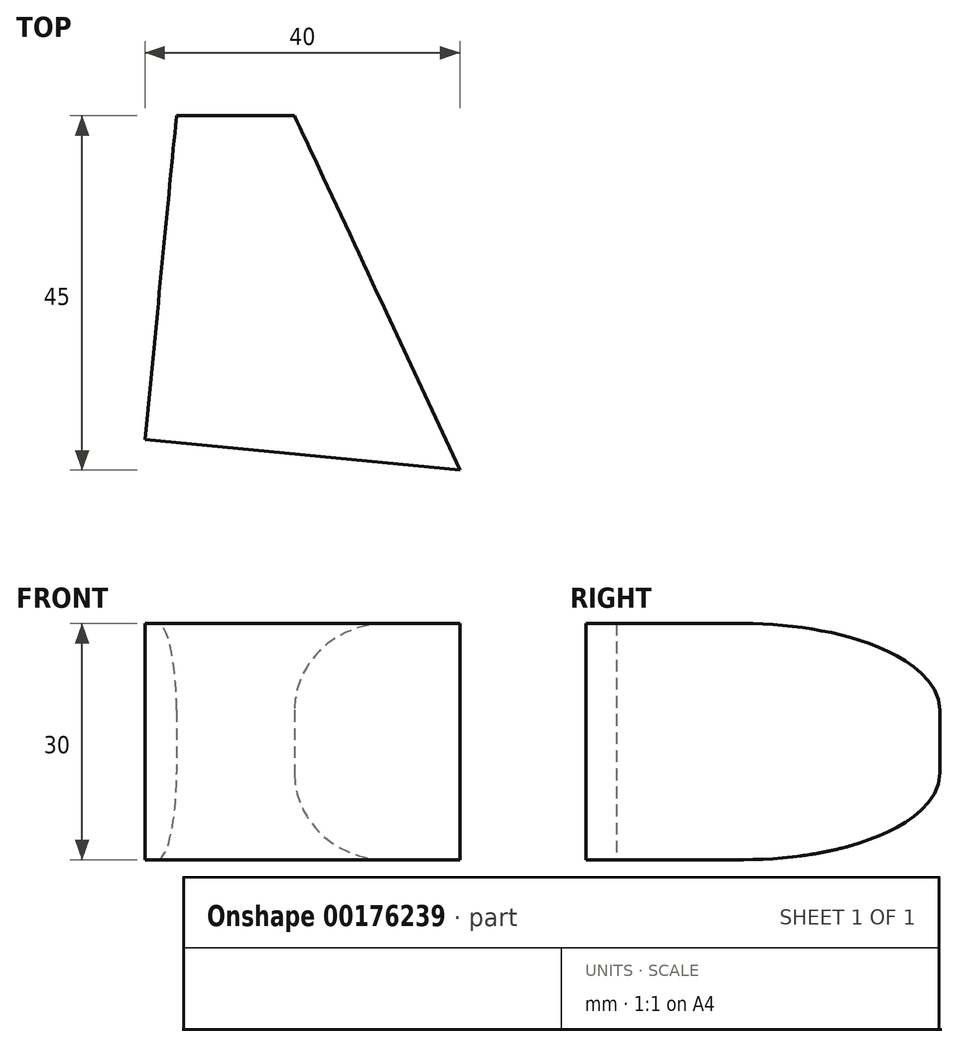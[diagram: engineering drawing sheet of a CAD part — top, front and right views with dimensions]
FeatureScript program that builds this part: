
annotation { "Feature Type Name" : "Feature", "Feature Type Description" : "" }
export const myFeature = defineFeature(function(context is Context, id is Id, definition is map)
    precondition{}
    {
        {
            var Q0;
            Q0=qCreatedBy(makeId("Top.planeOp"),FACE);
            var sketch = newSketch(context, id + "F0", { "sketchPlane" : qUnion([Q0])});
            skLineSegment(sketch, "E0", {"start": v(0, 20) * mm, "end": v(-15, 20) * mm});
            skLineSegment(sketch, "E1", {"start": v(-15, 20) * mm, "end": v(-19, -21.1) * mm});
            skLineSegment(sketch, "E2", {"start": v(-19, -21.1) * mm, "end": v(21, -25) * mm});
            skLineSegment(sketch, "E3", {"start": v(21, -25) * mm, "end": v(0, 20) * mm});
            skSolve(sketch);
        }
        {
            var Q0;
            Q0=qSketchRegion(id+"F0",true);
            extrude(context, id + "F1", {"entities" : qUnion([Q0]), "depth" : 15 * mm, "hasSecondDirection" : true, "secondDirectionOppositeDirection" : true, "secondDirectionDepth" : 15 * mm});
        }
        {
            var Q0;
            Q0=qCreatedBy(makeId("Right.planeOp"),FACE);
            var sketch = newSketch(context, id + "F2", { "sketchPlane" : qUnion([Q0])});
            skEllipticalArc(sketch, "E4", {});
            skLineSegment(sketch, "E5.0", {"start": v(20, 15) * mm, "end": v(20, -15) * mm, "construction": true});
            skPoint(sketch, "E6", {"position": v(20, -4) * mm});
            skPoint(sketch, "E7", {"position": v(-5, -15) * mm});
            skLineSegment(sketch, "E8", {"start": v(20, -4) * mm, "end": v(-5, -4) * mm, "construction": true});
            skLineSegment(sketch, "E9", {"start": v(-5, -15) * mm, "end": v(-5, -4) * mm, "construction": true});
            skEllipticalArc(sketch, "E10.MirrorCS", {});
            skLineSegment(sketch, "E11", {"start": v(-5, -15) * mm, "end": v(20, -15) * mm});
            skLineSegment(sketch, "E12", {"start": v(20, 15) * mm, "end": v(20, -15) * mm});
            skLineSegment(sketch, "E13", {"start": v(-5, 15) * mm, "end": v(20, 15) * mm});
            const initialGuessF2  = {"E4": [-0.005, -0.004, 1, 0, 0.025, 0.011, 4.71238898038469, 0], "E10.MirrorCS": [-0.005, 0.004, 1, 0, 0.025, 0.011, 0, 1.5707963267948966]};
            skSetInitialGuess(sketch, initialGuessF2);
            skSolve(sketch);
        }
        {
            var Q0;
            Q0=qSketchRegion(id+"F2",true);
            extrude(context, id + "F3", {"entities" : qUnion([Q0]), "operationType" : NewBodyOperationType.REMOVE, "endBound" : BoundingType.THROUGH_ALL, "oppositeDirection" : true, "depth" : 25 * mm, "hasSecondDirection" : true, "secondDirectionBound" : SecondDirectionBoundingType.THROUGH_ALL, "secondDirectionOppositeDirection" : false, "secondDirectionDepth" : 25 * mm});
        }
    });
